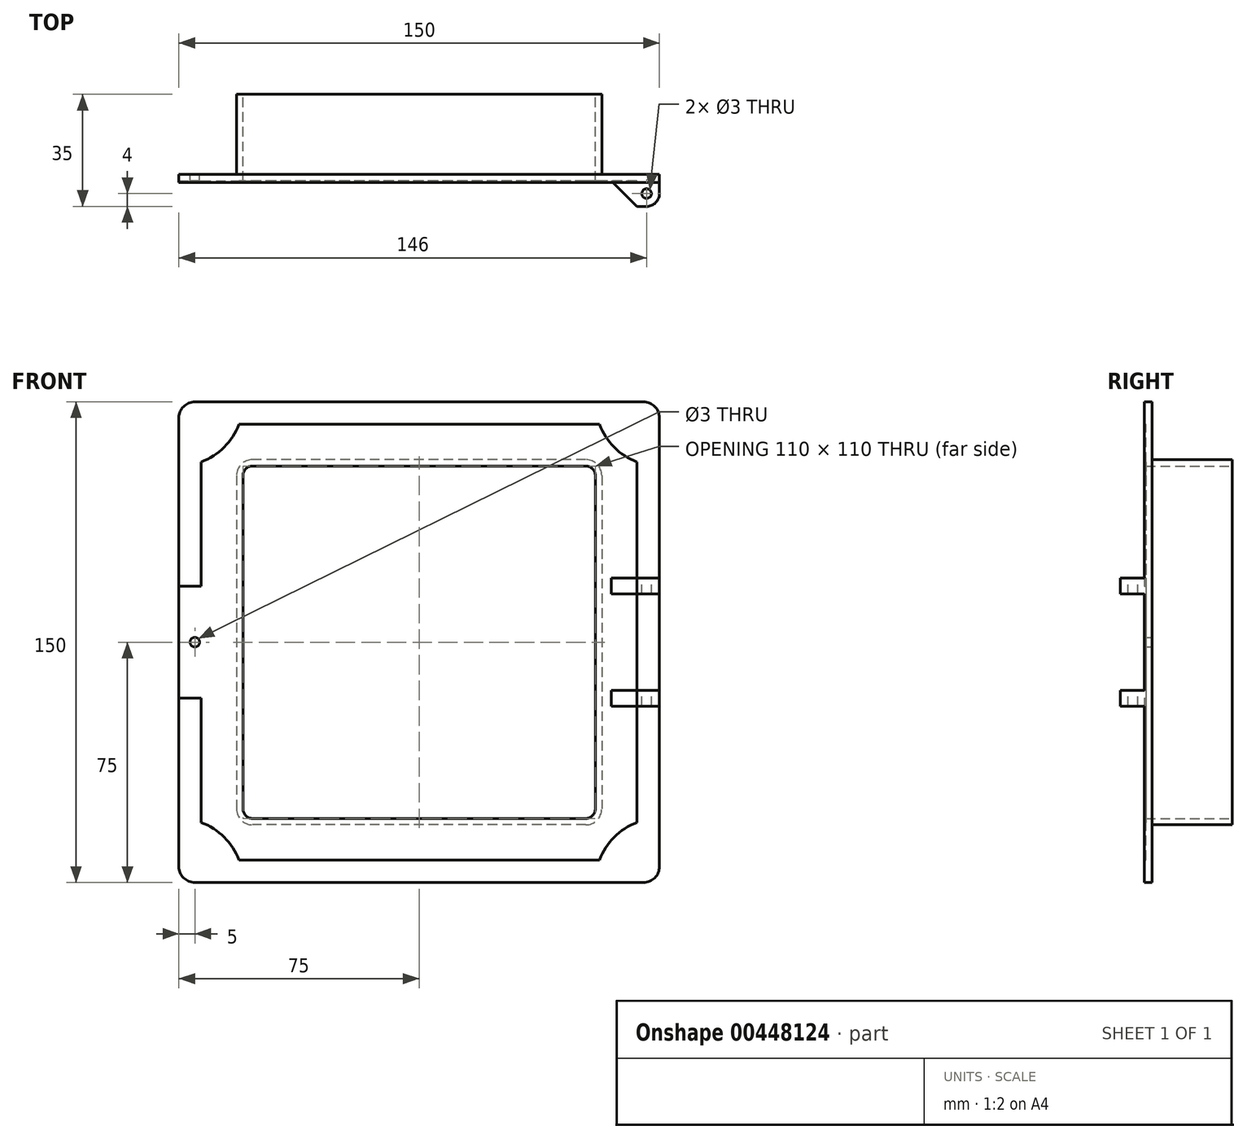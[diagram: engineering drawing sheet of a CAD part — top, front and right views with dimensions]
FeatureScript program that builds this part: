
annotation { "Feature Type Name" : "Feature", "Feature Type Description" : "" }
export const myFeature = defineFeature(function(context is Context, id is Id, definition is map)
    precondition{}
    {
        {
            var Q0;
            Q0=qCreatedBy(makeId("Front.planeOp"),FACE);
            var sketch = newSketch(context, id + "F0", { "sketchPlane" : qUnion([Q0])});
            skLineSegment(sketch, "E0.bottom", {"start": v(75, 75) * mm, "end": v(-75, 75) * mm});
            skLineSegment(sketch, "E0.top", {"start": v(75, -75) * mm, "end": v(-75, -75) * mm});
            skLineSegment(sketch, "E0.left", {"start": v(75, 75) * mm, "end": v(75, -75) * mm});
            skLineSegment(sketch, "E0.right", {"start": v(-75, 75) * mm, "end": v(-75, -75) * mm});
            skPoint(sketch, "E0.middle", {"position": v(0, 0) * mm});
            skLineSegment(sketch, "E1.bottom", {"start": v(55, 55) * mm, "end": v(-55, 55) * mm});
            skLineSegment(sketch, "E1.top", {"start": v(55, -55) * mm, "end": v(-55, -55) * mm});
            skLineSegment(sketch, "E1.left", {"start": v(55, 55) * mm, "end": v(55, -55) * mm});
            skLineSegment(sketch, "E1.right", {"start": v(-55, 55) * mm, "end": v(-55, -55) * mm});
            skLineSegment(sketch, "E2.0", {"start": v(68, 68) * mm, "end": v(-68, 68) * mm});
            skLineSegment(sketch, "E2.1", {"start": v(68, 68) * mm, "end": v(68, -68) * mm});
            skLineSegment(sketch, "E2.2", {"start": v(68, -68) * mm, "end": v(-68, -68) * mm});
            skLineSegment(sketch, "E2.3", {"start": v(-68, 68) * mm, "end": v(-68, 17.5) * mm});
            skLineSegment(sketch, "E3", {"start": v(-75, 17.5) * mm, "end": v(-68, 17.5) * mm});
            skLineSegment(sketch, "E4", {"start": v(-75, -17.5) * mm, "end": v(-68, -17.5) * mm});
            skLineSegment(sketch, "E5.trimOffspring", {"start": v(-68, -17.5) * mm, "end": v(-68, -68) * mm});
            skArc(sketch, "E6", {"start": v(-68, 56.27) * mm, "mid": v(-60.86, 60.86) * mm, "end": v(-56.27, 68) * mm});
            skArc(sketch, "E7", {"start": v(56.27, 68) * mm, "mid": v(60.86, 60.86) * mm, "end": v(68, 56.27) * mm});
            skArc(sketch, "E8", {"start": v(68, -56.27) * mm, "mid": v(60.86, -60.86) * mm, "end": v(56.27, -68) * mm});
            skArc(sketch, "E9", {"start": v(-56.27, -68) * mm, "mid": v(-60.86, -60.86) * mm, "end": v(-68, -56.27) * mm});
            skLineSegment(sketch, "E10.0", {"start": v(57, 57) * mm, "end": v(-57, 57) * mm});
            skLineSegment(sketch, "E10.1", {"start": v(57, 57) * mm, "end": v(57, -57) * mm});
            skLineSegment(sketch, "E10.2", {"start": v(57, -57) * mm, "end": v(-57, -57) * mm});
            skLineSegment(sketch, "E10.3", {"start": v(-57, 57) * mm, "end": v(-57, -57) * mm});
            skLineSegment(sketch, "E11", {"start": v(75, 20) * mm, "end": v(60, 20) * mm});
            skLineSegment(sketch, "E12", {"start": v(60, 20) * mm, "end": v(60, 15) * mm});
            skLineSegment(sketch, "E13", {"start": v(60, 15) * mm, "end": v(75, 15) * mm});
            skLineSegment(sketch, "E14", {"start": v(75, -15) * mm, "end": v(60, -15) * mm});
            skLineSegment(sketch, "E15", {"start": v(60, -15) * mm, "end": v(60, -20) * mm});
            skLineSegment(sketch, "E16", {"start": v(60, -20) * mm, "end": v(75, -20) * mm});
            skCircle(sketch, "E17", {"center": v(-70, 0) * mm, "radius": 1.5 * mm});
            skPoint(sketch, "E17.centerSnap0", {"position": v(-55, 0) * mm});
            skSolve(sketch);
        }
        {
            var Q0;
            {var subQ3=sQuery(id+"F0.wireOp",EDGE,"E3");Q0=makeQuery(id+"F0.imprint","IMPRINT",FACE,{"disambiguationData":[TD([[makeQuery(id+"F0.imprint","IMPRINT",EDGE,{"derivedFrom":subQ3}),-1.0]])]});}
            var Q1;
            Q1=makeQuery(id+"F0.imprint","IMPRINT",FACE,{"disambiguationData":[TD([[makeQuery(id+"F0.imprint","IMPRINT",EDGE,{"derivedFrom":sQuery(id+"F0.wireOp",EDGE,"E1.bottom")}),-1.0]])]});
            extrude(context, id + "F1", {"entities" : qUnion([Q0, Q1]), "depth" : 2 * mm});
        }
        {
            var Q0;
            {var subQ3=sQuery(id+"F0.wireOp",EDGE,"E6");Q0=makeQuery(id+"F0.imprint","IMPRINT",FACE,{"disambiguationData":[TD([[makeQuery(id+"F0.imprint","IMPRINT",EDGE,{"derivedFrom":subQ3}),1.0]])]});}
            var Q1;
            {var subQ12=sQuery(id+"F0.wireOp",EDGE,"E0.bottom");Q1=makeQuery(id+"F0.imprint","IMPRINT",FACE,{"disambiguationData":[TD([[makeQuery(id+"F0.imprint","IMPRINT",EDGE,{"derivedFrom":subQ12}),1.0]])]});}
            var Q2;
            {var subQ3=sQuery(id+"F0.wireOp",EDGE,"E7");Q2=makeQuery(id+"F0.imprint","IMPRINT",FACE,{"disambiguationData":[TD([[makeQuery(id+"F0.imprint","IMPRINT",EDGE,{"derivedFrom":subQ3}),1.0]])]});}
            var Q3;
            {var subQ3=sQuery(id+"F0.wireOp",EDGE,"E8");Q3=makeQuery(id+"F0.imprint","IMPRINT",FACE,{"disambiguationData":[TD([[makeQuery(id+"F0.imprint","IMPRINT",EDGE,{"derivedFrom":subQ3}),1.0]])]});}
            var Q4;
            {var subQ3=sQuery(id+"F0.wireOp",EDGE,"E9");Q4=makeQuery(id+"F0.imprint","IMPRINT",FACE,{"disambiguationData":[TD([[makeQuery(id+"F0.imprint","IMPRINT",EDGE,{"derivedFrom":subQ3}),1.0]])]});}
            var Q5;
            {var subQ10=sQuery(id+"F0.wireOp",EDGE,"E0.top");Q5=makeQuery(id+"F0.imprint","IMPRINT",FACE,{"disambiguationData":[TD([[makeQuery(id+"F0.imprint","IMPRINT",EDGE,{"derivedFrom":subQ10}),-1.0]])]});}
            var Q6;
            {var subQ0=sQuery(id+"F0.wireOp",EDGE,"E13");var subQ1=sQuery(id+"F0.wireOp",EDGE,"E0.left");var subQ2=makeQuery(id+"F0.imprint","INTERSECT",VERTEX,{"derivedFrom":[subQ1,subQ0]});Q6=makeQuery(id+"F0.imprint","IMPRINT",FACE,{"disambiguationData":[TD([[makeQuery(id+"F0.imprint","IMPRINT",EDGE,{"disambiguationData":[TD([[subQ2,-1.0]])],"derivedFrom":subQ1}),-1.0]])]});}
            extrude(context, id + "F2", {"entities" : qUnion([Q0, Q1, Q2, Q3, Q4, Q5, Q6]), "operationType" : NewBodyOperationType.ADD, "depth" : 2.5 * mm});
        }
        {
            var Q0;
            {var subQ0=sQuery(id+"F0.wireOp",EDGE,"E11");var subQ1=sQuery(id+"F0.wireOp",EDGE,"E0.left");var subQ2=makeQuery(id+"F0.imprint","INTERSECT",VERTEX,{"derivedFrom":[subQ1,subQ0]});Q0=makeQuery(id+"F0.imprint","IMPRINT",FACE,{"disambiguationData":[TD([[makeQuery(id+"F0.imprint","IMPRINT",EDGE,{"disambiguationData":[TD([[subQ2,-1.0]])],"derivedFrom":subQ1}),-1.0]])]});}
            var Q1;
            {var subQ5=sQuery(id+"F0.wireOp",EDGE,"E12");Q1=makeQuery(id+"F0.imprint","IMPRINT",FACE,{"disambiguationData":[TD([[makeQuery(id+"F0.imprint","IMPRINT",EDGE,{"derivedFrom":subQ5}),1.0]])]});}
            var Q2;
            {var subQ5=sQuery(id+"F0.wireOp",EDGE,"E15");Q2=makeQuery(id+"F0.imprint","IMPRINT",FACE,{"disambiguationData":[TD([[makeQuery(id+"F0.imprint","IMPRINT",EDGE,{"derivedFrom":subQ5}),1.0]])]});}
            var Q3;
            {var subQ0=sQuery(id+"F0.wireOp",EDGE,"E14");var subQ1=sQuery(id+"F0.wireOp",EDGE,"E0.left");var subQ2=makeQuery(id+"F0.imprint","INTERSECT",VERTEX,{"derivedFrom":[subQ1,subQ0]});Q3=makeQuery(id+"F0.imprint","IMPRINT",FACE,{"disambiguationData":[TD([[makeQuery(id+"F0.imprint","IMPRINT",EDGE,{"disambiguationData":[TD([[subQ2,-1.0]])],"derivedFrom":subQ1}),-1.0]])]});}
            extrude(context, id + "F3", {"entities" : qUnion([Q0, Q1, Q2, Q3]), "operationType" : NewBodyOperationType.ADD, "depth" : 10 * mm});
        }
        {
            var Q0;
            Q0=makeQuery(id+"F3.opExtrude","CAP_EDGE",EDGE,{"disambiguationData":[OSD([sQuery(id+"F0.wireOp",EDGE,"E12")])],"isStart":false});
            var Q1;
            Q1=makeQuery(id+"F3.opExtrude","CAP_EDGE",EDGE,{"disambiguationData":[OSD([sQuery(id+"F0.wireOp",EDGE,"E15")])],"isStart":false});
            chamfer(context, id + "F4", {"entities" : qUnion([Q0, Q1]), "width" : 8 * mm, "tangentPropagation" : true});
        }
        {
            var Q0;
            {var subQ0=sQuery(id+"F0.wireOp",EDGE,"E0.left");Q0=makeQuery(id+"F3.opExtrude","CAP_EDGE",EDGE,{"disambiguationData":[OSD([subQ0]),TDD([makeQuery(id+"F0.imprint","IMPRINT",EDGE,{"disambiguationData":[TD([[makeQuery(id+"F0.imprint","INTERSECT",VERTEX,{"derivedFrom":[subQ0,sQuery(id+"F0.wireOp",EDGE,"E11")]}),-1.0]])],"derivedFrom":subQ0})])],"isStart":false});}
            var Q1;
            {var subQ0=sQuery(id+"F0.wireOp",EDGE,"E0.left");Q1=makeQuery(id+"F3.opExtrude","CAP_EDGE",EDGE,{"disambiguationData":[OSD([subQ0]),TDD([makeQuery(id+"F0.imprint","IMPRINT",EDGE,{"disambiguationData":[TD([[makeQuery(id+"F0.imprint","INTERSECT",VERTEX,{"derivedFrom":[subQ0,sQuery(id+"F0.wireOp",EDGE,"E14")]}),-1.0]])],"derivedFrom":subQ0})])],"isStart":false});}
            fillet(context, id + "F5", {"entities" : qUnion([Q0, Q1]), "radius" : 4 * mm, "tangentPropagation" : true, "allowEdgeOverflow" : false});
        }
        {
            var Q0;
            Q0=makeQuery(id+"F0.imprint","IMPRINT",FACE,{"disambiguationData":[TD([[makeQuery(id+"F0.imprint","IMPRINT",EDGE,{"derivedFrom":sQuery(id+"F0.wireOp",EDGE,"E1.bottom")}),-1.0]])]});
            extrude(context, id + "F6", {"entities" : qUnion([Q0]), "operationType" : NewBodyOperationType.ADD, "oppositeDirection" : true, "depth" : 25 * mm});
        }
        {
            var Q0;
            {var subQ0=sQuery(id+"F0.wireOp",EDGE,"E1.right");var subQ1=sQuery(id+"F0.wireOp",EDGE,"E1.bottom");Q0=makeQuery(id+"F6.boolean.opBoolean","MERGE",EDGE,{"derivedFrom":[makeQuery(id+"F1.opExtrude","SWEPT_EDGE",EDGE,{"disambiguationData":[OSD([subQ1,subQ0])]}),makeQuery(id+"F6.opExtrude","SWEPT_EDGE",EDGE,{"disambiguationData":[OSD([subQ1,subQ0])]})]});}
            var Q1;
            {var subQ0=sQuery(id+"F0.wireOp",EDGE,"E1.left");var subQ1=sQuery(id+"F0.wireOp",EDGE,"E1.bottom");Q1=makeQuery(id+"F6.boolean.opBoolean","MERGE",EDGE,{"derivedFrom":[makeQuery(id+"F1.opExtrude","SWEPT_EDGE",EDGE,{"disambiguationData":[OSD([subQ1,subQ0])]}),makeQuery(id+"F6.opExtrude","SWEPT_EDGE",EDGE,{"disambiguationData":[OSD([subQ1,subQ0])]})]});}
            var Q2;
            {var subQ0=sQuery(id+"F0.wireOp",EDGE,"E1.left");var subQ1=sQuery(id+"F0.wireOp",EDGE,"E1.top");Q2=makeQuery(id+"F6.boolean.opBoolean","MERGE",EDGE,{"derivedFrom":[makeQuery(id+"F1.opExtrude","SWEPT_EDGE",EDGE,{"disambiguationData":[OSD([subQ1,subQ0])]}),makeQuery(id+"F6.opExtrude","SWEPT_EDGE",EDGE,{"disambiguationData":[OSD([subQ1,subQ0])]})]});}
            var Q3;
            {var subQ0=sQuery(id+"F0.wireOp",EDGE,"E1.right");var subQ1=sQuery(id+"F0.wireOp",EDGE,"E1.top");Q3=makeQuery(id+"F6.boolean.opBoolean","MERGE",EDGE,{"derivedFrom":[makeQuery(id+"F1.opExtrude","SWEPT_EDGE",EDGE,{"disambiguationData":[OSD([subQ1,subQ0])]}),makeQuery(id+"F6.opExtrude","SWEPT_EDGE",EDGE,{"disambiguationData":[OSD([subQ1,subQ0])]})]});}
            fillet(context, id + "F7", {"entities" : qUnion([Q0, Q1, Q2, Q3]), "radius" : 3 * mm, "tangentPropagation" : true, "allowEdgeOverflow" : false});
        }
        {
            var Q0;
            Q0=makeQuery(id+"F6.opExtrude","SWEPT_EDGE",EDGE,{"disambiguationData":[OSD([sQuery(id+"F0.wireOp",EDGE,"E10.0"),sQuery(id+"F0.wireOp",EDGE,"E10.1")])]});
            var Q1;
            Q1=makeQuery(id+"F6.opExtrude","SWEPT_EDGE",EDGE,{"disambiguationData":[OSD([sQuery(id+"F0.wireOp",EDGE,"E10.1"),sQuery(id+"F0.wireOp",EDGE,"E10.2")])]});
            var Q2;
            Q2=makeQuery(id+"F6.opExtrude","SWEPT_EDGE",EDGE,{"disambiguationData":[OSD([sQuery(id+"F0.wireOp",EDGE,"E10.2"),sQuery(id+"F0.wireOp",EDGE,"E10.3")])]});
            var Q3;
            Q3=makeQuery(id+"F6.opExtrude","SWEPT_EDGE",EDGE,{"disambiguationData":[OSD([sQuery(id+"F0.wireOp",EDGE,"E10.0"),sQuery(id+"F0.wireOp",EDGE,"E10.3")])]});
            var Q4;
            Q4=makeQuery(id+"F2.opExtrude","SWEPT_EDGE",EDGE,{"disambiguationData":[OSD([sQuery(id+"F0.wireOp",EDGE,"E0.bottom"),sQuery(id+"F0.wireOp",EDGE,"E0.right")])]});
            var Q5;
            Q5=makeQuery(id+"F2.opExtrude","SWEPT_EDGE",EDGE,{"disambiguationData":[OSD([sQuery(id+"F0.wireOp",EDGE,"E0.top"),sQuery(id+"F0.wireOp",EDGE,"E0.right")])]});
            var Q6;
            Q6=makeQuery(id+"F2.opExtrude","SWEPT_EDGE",EDGE,{"disambiguationData":[OSD([sQuery(id+"F0.wireOp",EDGE,"E0.top"),sQuery(id+"F0.wireOp",EDGE,"E0.left")])]});
            var Q7;
            Q7=makeQuery(id+"F2.opExtrude","SWEPT_EDGE",EDGE,{"disambiguationData":[OSD([sQuery(id+"F0.wireOp",EDGE,"E0.bottom"),sQuery(id+"F0.wireOp",EDGE,"E0.left")])]});
            fillet(context, id + "F8", {"entities" : qUnion([Q0, Q1, Q2, Q3, Q4, Q5, Q6, Q7]), "radius" : 5 * mm, "tangentPropagation" : true, "allowEdgeOverflow" : false});
        }
        {
            var Q0;
            Q0=makeQuery(id+"F3.opExtrude","SWEPT_FACE",FACE,{"disambiguationData":[OSD([sQuery(id+"F0.wireOp",EDGE,"E11")])]});
            var sketch = newSketch(context, id + "F9", { "sketchPlane" : qUnion([Q0])});
            skPoint(sketch, "E18", {"position": v(71, -6) * mm});
            skSolve(sketch);
        }
        {
            var Q0;
            Q0=sQuery(id+"F9.wireOp",VERTEX,"E18");
            var Q1;
            Q1=makeQuery(id+"F1.opExtrude","SWEPT_BODY",BODY,{"disambiguationData":[OSD([sQuery(id+"F0.wireOp",EDGE,"E0.right"),sQuery(id+"F0.wireOp",EDGE,"E1.bottom"),sQuery(id+"F0.wireOp",EDGE,"E1.top"),sQuery(id+"F0.wireOp",EDGE,"E1.left"),sQuery(id+"F0.wireOp",EDGE,"E1.right"),sQuery(id+"F0.wireOp",EDGE,"E2.0"),sQuery(id+"F0.wireOp",EDGE,"E2.1"),sQuery(id+"F0.wireOp",EDGE,"E2.2"),sQuery(id+"F0.wireOp",EDGE,"E2.3"),sQuery(id+"F0.wireOp",EDGE,"E3"),sQuery(id+"F0.wireOp",EDGE,"E4"),sQuery(id+"F0.wireOp",EDGE,"E5.trimOffspring"),sQuery(id+"F0.wireOp",EDGE,"E6"),sQuery(id+"F0.wireOp",EDGE,"E7"),sQuery(id+"F0.wireOp",EDGE,"E8"),sQuery(id+"F0.wireOp",EDGE,"E9"),sQuery(id+"F0.wireOp",EDGE,"E11"),sQuery(id+"F0.wireOp",EDGE,"E12"),sQuery(id+"F0.wireOp",EDGE,"E13"),sQuery(id+"F0.wireOp",EDGE,"E14"),sQuery(id+"F0.wireOp",EDGE,"E15"),sQuery(id+"F0.wireOp",EDGE,"E16")])]});
            hole(context, id + "F10", {"style" : HoleStyle.SIMPLE, "endStyle" : HoleEndStyle.THROUGH, "holeDiameter" : 3 * mm, "isTappedThrough" : true, "tappedDepth" : 12 * mm, "tapClearance" : 3, "locations" : qUnion([Q0]), "scope" : qUnion([Q1])});
        }
    });
